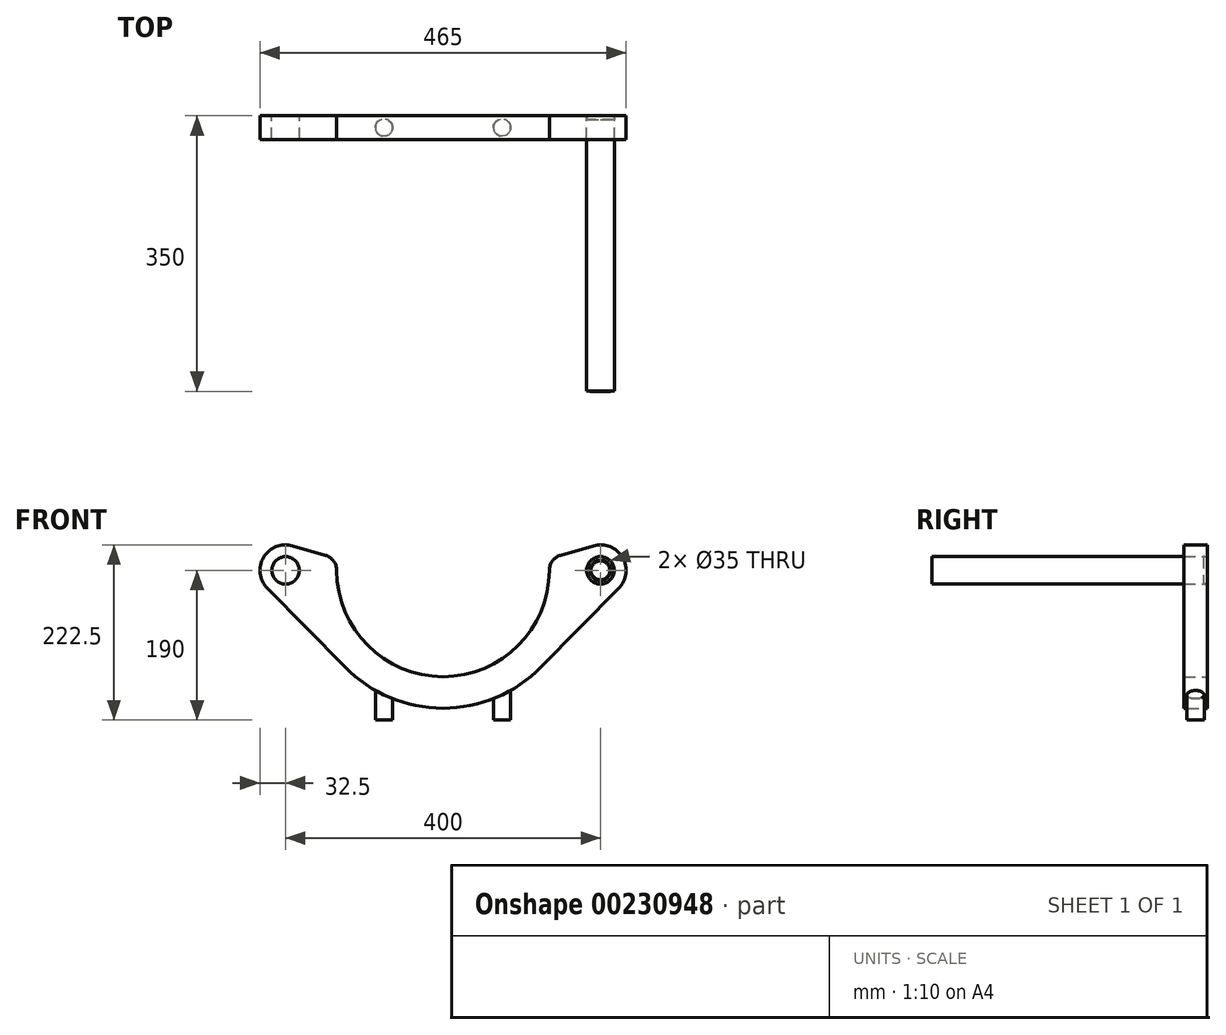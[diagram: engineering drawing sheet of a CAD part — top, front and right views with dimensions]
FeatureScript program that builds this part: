
annotation { "Feature Type Name" : "Feature", "Feature Type Description" : "" }
export const myFeature = defineFeature(function(context is Context, id is Id, definition is map)
    precondition{}
    {
        {
            var Q0;
            Q0=qCreatedBy(makeId("Front.planeOp"),FACE);
            var sketch = newSketch(context, id + "F0", { "sketchPlane" : qUnion([Q0])});
            skLineSegment(sketch, "E0", {"start": v(0, 133.34) * mm, "end": v(0, -25.28) * mm, "construction": true});
            skLineSegment(sketch, "E1", {"start": v(-296.41, 0) * mm, "end": v(271.16, 0) * mm, "construction": true});
            skCircle(sketch, "E2", {"center": v(0, 0) * mm, "radius": 125 * mm, "construction": true});
            skSolve(sketch);
        }
        {
            var Q0;
            Q0=qCreatedBy(makeId("Front.planeOp"),FACE);
            var sketch = newSketch(context, id + "F1", { "sketchPlane" : qUnion([Q0])});
            skArc(sketch, "E3", {"start": v(-135, 0) * mm, "mid": v(0, -135) * mm, "end": v(135, 0) * mm});
            skArc(sketch, "E4", {"start": v(-124.69, -122.8) * mm, "mid": v(0, -175) * mm, "end": v(124.69, -122.8) * mm});
            skCircle(sketch, "E5", {"center": v(200, 0) * mm, "radius": 17.5 * mm});
            skCircle(sketch, "E6", {"center": v(-200, 0) * mm, "radius": 17.5 * mm});
            skLineSegment(sketch, "E7", {"start": v(-223.16, -22.8) * mm, "end": v(-124.69, -122.8) * mm});
            skLineSegment(sketch, "E8", {"start": v(124.69, -122.8) * mm, "end": v(223.16, -22.8) * mm});
            skArc(sketch, "E9", {"start": v(-190.97, 31.22) * mm, "mid": v(-227.92, 16.63) * mm, "end": v(-223.16, -22.8) * mm});
            skArc(sketch, "E10", {"start": v(223.16, -22.8) * mm, "mid": v(227.92, 16.63) * mm, "end": v(190.97, 31.22) * mm});
            skPoint(sketch, "E11.orphan", {"position": v(-245.61, 0) * mm});
            skPoint(sketch, "E12.orphan", {"position": v(245.61, 0) * mm});
            skArc(sketch, "E13", {"start": v(-135, 0) * mm, "mid": v(-139.01, 12.02) * mm, "end": v(-149.44, 19.21) * mm});
            skArc(sketch, "E14", {"start": v(149.44, 19.21) * mm, "mid": v(139.01, 12.02) * mm, "end": v(135, 0) * mm});
            skLineSegment(sketch, "E15", {"start": v(-149.44, 19.21) * mm, "end": v(-190.97, 31.22) * mm});
            skLineSegment(sketch, "E16", {"start": v(149.44, 19.21) * mm, "end": v(190.97, 31.22) * mm});
            skSolve(sketch);
        }
        {
            var Q0;
            Q0 = qSketchRegion(id + "F1", true);
            extrude(context, id + "F2", {"entities" : qUnion([Q0]), "depth" : 30 * mm, "symmetric" : true});
        }
        {
            var Q0;
            Q0=qCreatedBy(makeId("Top.planeOp"),FACE);
            cPlane(context, id + "F3", {"entities" : qUnion([Q0]), "cplaneType" : CPlaneType.OFFSET, "offset" : 190 * mm, "oppositeDirection" : true, "width" : 150 * mm, "height" : 150 * mm});
        }
        {
            var Q0;
            Q0=qCreatedBy(id+"F3.planeOp",FACE);
            var sketch = newSketch(context, id + "F4", { "sketchPlane" : qUnion([Q0])});
            skCircle(sketch, "E17", {"center": v(-75, 0) * mm, "radius": 11 * mm});
            skCircle(sketch, "E18", {"center": v(75, 0) * mm, "radius": 11 * mm});
            skSolve(sketch);
        }
        {
            var Q0;
            Q0 = qSketchRegion(id + "F4", true);
            extrude(context, id + "F5", {"entities" : qUnion([Q0]), "operationType" : NewBodyOperationType.ADD, "depth" : 45 * mm});
        }
        {
            var Q0;
            Q0=makeQuery(id+"F2.opExtrude","CAP_FACE",FACE,{"disambiguationData":[OSD([sQuery(id+"F1.wireOp",EDGE,"E3"),sQuery(id+"F1.wireOp",EDGE,"E4"),sQuery(id+"F1.wireOp",EDGE,"E5"),sQuery(id+"F1.wireOp",EDGE,"E6"),sQuery(id+"F1.wireOp",EDGE,"E7"),sQuery(id+"F1.wireOp",EDGE,"E8"),sQuery(id+"F1.wireOp",EDGE,"E9"),sQuery(id+"F1.wireOp",EDGE,"E10"),sQuery(id+"F1.wireOp",EDGE,"E13"),sQuery(id+"F1.wireOp",EDGE,"E14"),sQuery(id+"F1.wireOp",EDGE,"E15"),sQuery(id+"F1.wireOp",EDGE,"E16")])],"isStart":true});
            var sketch = newSketch(context, id + "F6", { "sketchPlane" : qUnion([Q0])});
            skCircle(sketch, "E19", {"center": v(-200, 0) * mm, "radius": 17.5 * mm});
            skSolve(sketch);
        }
        {
            var Q0;
            Q0 = qSketchRegion(id + "F6", true);
            extrude(context, id + "F7", {"entities" : qUnion([Q0]), "oppositeDirection" : true, "depth" : 350 * mm});
        }
        {
            var Q0;
            Q0=makeQuery(id+"F7.opExtrude","CAP_FACE",FACE,{"disambiguationData":[OSD([sQuery(id+"F6.wireOp",EDGE,"E19")])],"isStart":true});
            chamfer(context, id + "F8", {"entities" : qUnion([Q0]), "chamferType" : ChamferType.OFFSET_ANGLE, "width" : 5 * mm, "oppositeDirection" : false, "angle" : 5 * degree, "tangentPropagation" : true});
        }
        {
            var Q0;
            {var subQ0=sQuery(id+"F6.wireOp",EDGE,"E19");Q0=makeQuery(id+"F8.opChamfer","BLEND_EDGE",EDGE,{"blendedFrom":[makeQuery(id+"F7.opExtrude","CAP_EDGE",EDGE,{"disambiguationData":[OSD([subQ0])],"isStart":true}),makeQuery(id+"F7.opExtrude","CAP_FACE",FACE,{"disambiguationData":[OSD([subQ0])],"isStart":true})],"blendedInto":[makeQuery(id+"F7.opExtrude","CAP_FACE",FACE,{"disambiguationData":[OSD([subQ0])],"isStart":true})]});}
            chamfer(context, id + "F9", {"entities" : qUnion([Q0]), "width" : .5 * mm, "tangentPropagation" : true});
        }
        {
            var Q0;
            Q0=makeQuery(id+"F7.opExtrude","CAP_EDGE",EDGE,{"disambiguationData":[OSD([sQuery(id+"F6.wireOp",EDGE,"E19")])],"isStart":false});
            chamfer(context, id + "F10", {"entities" : qUnion([Q0]), "chamferType" : ChamferType.OFFSET_ANGLE, "width" : 5 * mm, "oppositeDirection" : true, "angle" : 5 * degree, "tangentPropagation" : true});
        }
        {
            var Q0;
            {var subQ0=sQuery(id+"F6.wireOp",EDGE,"E19");Q0=makeQuery(id+"F10.opChamfer","BLEND_EDGE",EDGE,{"blendedFrom":[makeQuery(id+"F7.opExtrude","CAP_EDGE",EDGE,{"disambiguationData":[OSD([subQ0])],"isStart":false}),makeQuery(id+"F7.opExtrude","CAP_FACE",FACE,{"disambiguationData":[OSD([subQ0])],"isStart":false})],"blendedInto":[makeQuery(id+"F7.opExtrude","CAP_FACE",FACE,{"disambiguationData":[OSD([subQ0])],"isStart":false})]});}
            chamfer(context, id + "F11", {"entities" : qUnion([Q0]), "width" : .5 * mm, "tangentPropagation" : true});
        }
    });
